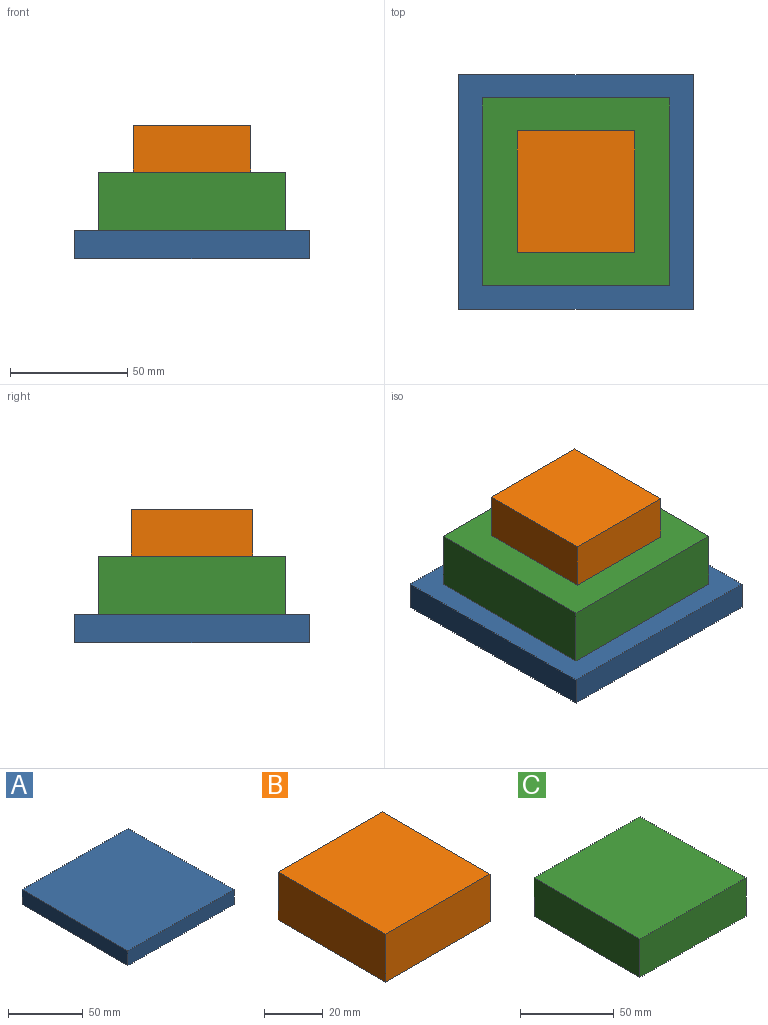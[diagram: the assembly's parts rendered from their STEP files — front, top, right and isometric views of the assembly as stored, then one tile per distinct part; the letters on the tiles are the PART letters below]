
ASSEMBLY  parts=3 mates=2
PART A: 6 faces, bbox 100x100x12 mm
  f0: plane 100x12mm, normal (1,0,0), area 1200mm2, adj f1,f3,f4,f5
  f1: plane 100x12mm, normal (0,1,0), area 1200mm2, adj f0,f2,f4,f5
  f2: plane 100x12mm, normal (-1,0,0), area 1200mm2, adj f1,f3,f4,f5
  f3: plane 100x12mm, normal (0,-1,0), area 1200mm2, adj f0,f2,f4,f5
  f4: plane 100x100mm, normal (0,0,1), area 10000mm2, adj f0,f1,f2,f3
  f5: plane 100x100mm, normal (0,0,-1), area 10000mm2, adj f0,f1,f2,f3
PART B: 6 faces, bbox 50.2x51.9x20 mm
  f0: plane 51.9x20mm, normal (1,0,0), area 1038.1mm2, adj f1,f3,f4,f5
  f1: plane 50.24x20mm, normal (0,1,0), area 1004.7mm2, adj f0,f2,f4,f5
  f2: plane 51.9x20mm, normal (-1,0,0), area 1038.1mm2, adj f1,f3,f4,f5
  f3: plane 50.24x20mm, normal (0,-1,0), area 1004.7mm2, adj f0,f2,f4,f5
  f4: plane 51.9x50.24mm, normal (0,0,1), area 2607.4mm2, adj f0,f1,f2,f3
  f5: plane 51.9x50.24mm, normal (0,0,-1), area 2607.4mm2, adj f0,f1,f2,f3
PART C: 6 faces, bbox 80x80x25 mm
  f0: plane 80x25mm, normal (1,0,0), area 2000mm2, adj f1,f3,f4,f5
  f1: plane 80x25mm, normal (0,1,0), area 2000mm2, adj f0,f2,f4,f5
  f2: plane 80x25mm, normal (-1,0,0), area 2000mm2, adj f1,f3,f4,f5
  f3: plane 80x25mm, normal (0,-1,0), area 2000mm2, adj f0,f2,f4,f5
  f4: plane 80x80mm, normal (0,0,1), area 6400mm2, adj f0,f1,f2,f3
  f5: plane 80x80mm, normal (0,0,-1), area 6400mm2, adj f0,f1,f2,f3
PLACE A t=(-9.64,-1.09,0.72)mm
PLACE B t=(-9.64,-1.09,37.72)mm
PLACE C t=(-9.64,-1.09,12.72)mm
MATE fastened C.f5 <-> A.f4  axis (0,0,-1) through (-9.64,-1.09,12.72)mm
MATE fastened B.f5 <-> C.f4  axis (0,0,-1) through (-9.64,-1.09,37.72)mm
